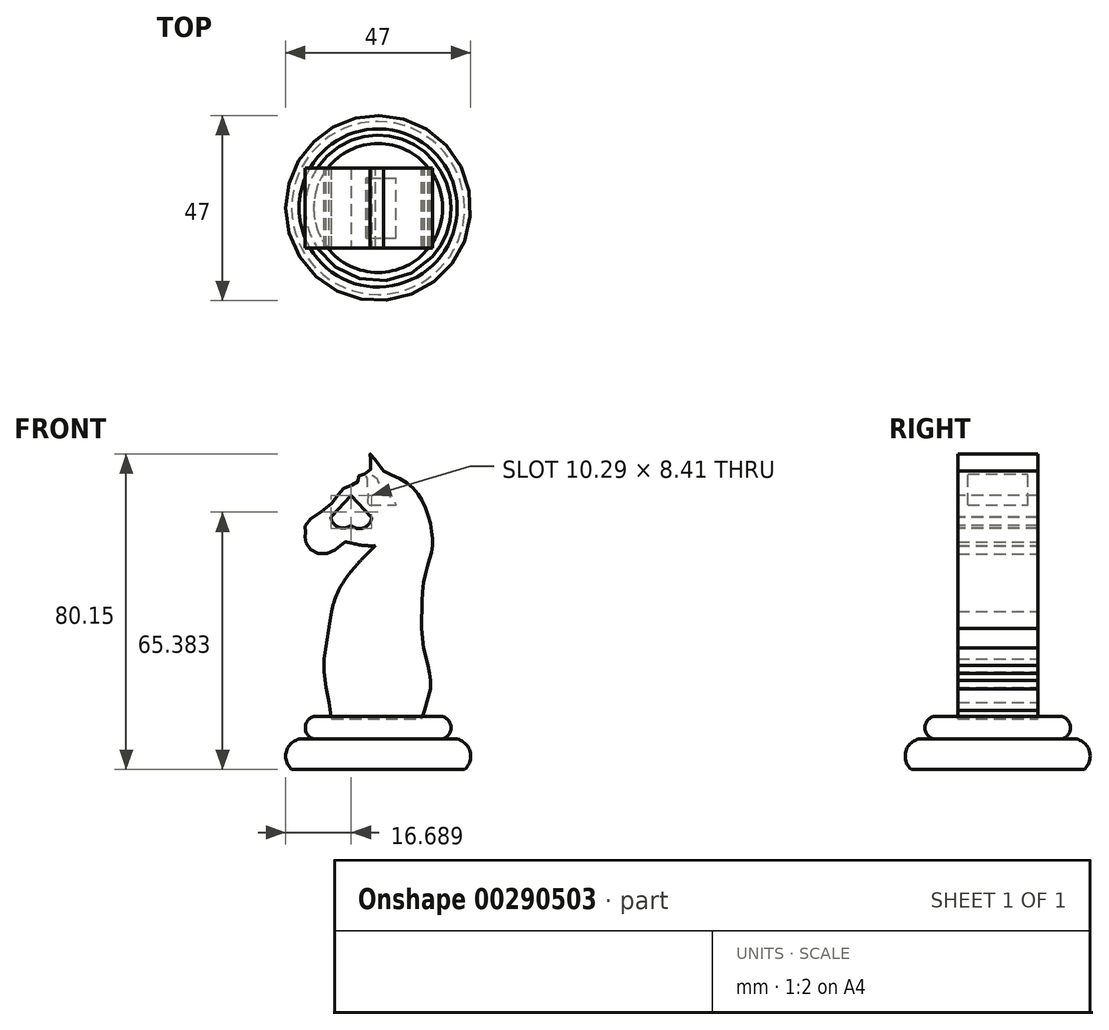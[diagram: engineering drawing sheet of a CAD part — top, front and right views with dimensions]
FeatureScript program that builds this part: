
annotation { "Feature Type Name" : "Feature", "Feature Type Description" : "" }
export const myFeature = defineFeature(function(context is Context, id is Id, definition is map)
    precondition{}
    {
        {
            var Q0;
            Q0=qCreatedBy(makeId("Front.planeOp"),FACE);
            var sketch = newSketch(context, id + "F0", { "sketchPlane" : qUnion([Q0])});
            skArc(sketch, "E0", {"start": v(-7.91, 12.56) * mm, "mid": v(-4.66, 11.9) * mm, "end": v(-2.68, 14.57) * mm});
            skArc(sketch, "E1", {"start": v(-12.98, 14.73) * mm, "mid": v(-11.11, 12.1) * mm, "end": v(-7.91, 12.56) * mm});
            skLineSegment(sketch, "E2", {"start": v(-2.68, 14.57) * mm, "end": v(-7.91, 20.12) * mm});
            skLineSegment(sketch, "E3", {"start": v(-7.91, 20.12) * mm, "end": v(-12.98, 14.73) * mm});
            skSolve(sketch);
        }
        {
            var Q0;
            Q0=qCreatedBy(makeId("Front.planeOp"),FACE);
            var sketch = newSketch(context, id + "F1", { "sketchPlane" : qUnion([Q0])});
            skFitSpline(sketch, "E4", {"points": [v(10.03, -13.65) * mm, v(10.07, -10.39) * mm, v(10.65, -1.4) * mm, v(12.36, 5) * mm, v(12.72, 10.14) * mm, v(11, 16.98) * mm, v(7.45, 22.46) * mm, v(0.32, 26.3) * mm], "startDerivative": vector(-2.98, 24.85) * mm, "endDerivative": vector(-48.92, 20.58) * mm});
            skPoint(sketch, "E5.2.internal.snap0", {"position": v(-3.12, 30.6) * mm});
            skFitSpline(sketch, "E5", {"points": [v(0.32, 26.3) * mm, v(-3.12, 30.6) * mm, v(-3.12, 26.3) * mm, v(-5.87, 25.2) * mm, v(-6.22, 23.55) * mm, v(-9.57, 22.05) * mm, v(-13.06, 17.92) * mm, v(-19.47, 12.65) * mm, v(-19.4, 10.51) * mm, v(-19.62, 9.3) * mm, v(-18.26, 6.45) * mm, v(-14.13, 5.38) * mm, v(-10.85, 7.16) * mm, v(-9.5, 8.23) * mm, v(-5.72, 7.59) * mm, v(-1.73, 7.38) * mm], "startDerivative": vector(-65.76, 86.9) * mm, "endDerivative": vector(54.48, 1.25) * mm});
            skLineSegment(sketch, "E6", {"start": v(-6.37, 2.6) * mm, "end": v(-9.5, 8.23) * mm});
            skLineSegment(sketch, "E7", {"start": v(-12.83, -36.6) * mm, "end": v(10.03, -36.6) * mm});
            skLineSegment(sketch, "E8", {"start": v(-12.83, -9.3) * mm, "end": v(-13.43, -13.22) * mm});
            skLineSegment(sketch, "E9", {"start": v(-13.43, -13.22) * mm, "end": v(-14.7, -21.38) * mm});
            skLineSegment(sketch, "E10", {"start": v(-14.7, -21.38) * mm, "end": v(-14.7, -24.75) * mm});
            skLineSegment(sketch, "E11", {"start": v(-14.7, -24.75) * mm, "end": v(-14.23, -28.6) * mm});
            skLineSegment(sketch, "E12", {"start": v(-14.23, -28.6) * mm, "end": v(-13.54, -32.4) * mm});
            skLineSegment(sketch, "E13", {"start": v(-13.54, -32.4) * mm, "end": v(-12.83, -36.6) * mm});
            skLineSegment(sketch, "E14", {"start": v(12.04, -25.03) * mm, "end": v(11.65, -23.06) * mm});
            skLineSegment(sketch, "E15", {"start": v(11.65, -23.06) * mm, "end": v(10.56, -18.55) * mm});
            skLineSegment(sketch, "E16", {"start": v(10.56, -18.55) * mm, "end": v(10.03, -13.65) * mm});
            skFitSpline(sketch, "E17", {"points": [v(-12.83, -9.3) * mm, v(-11.29, -4.57) * mm, v(-9.35, -1.12) * mm, v(-6.37, 2.6) * mm, v(-1.73, 7.38) * mm], "startDerivative": vector(1.98, 16.57) * mm, "endDerivative": vector(17.28, 17.22) * mm});
            skLineSegment(sketch, "E18", {"start": v(10.03, -36.6) * mm, "end": v(10.76, -34.51) * mm});
            skLineSegment(sketch, "E19", {"start": v(10.76, -34.51) * mm, "end": v(12.24, -29.07) * mm});
            skLineSegment(sketch, "E20", {"start": v(12.24, -29.07) * mm, "end": v(12.24, -26.82) * mm});
            skLineSegment(sketch, "E21", {"start": v(12.24, -26.82) * mm, "end": v(12.04, -25.03) * mm});
            skSolve(sketch);
        }
        {
            var Q0;
            Q0=makeQuery(id+"F1.imprint","IMPRINT",FACE,{"disambiguationData":[TD([[makeQuery(id+"F1.imprint","IMPRINT",EDGE,{"derivedFrom":sQuery(id+"F1.wireOp",EDGE,"E4")}),1.0]])]});
            extrude(context, id + "F2", {"entities" : qUnion([Q0]), "endBound" : BoundingType.SYMMETRIC, "depth" : 20.32 * mm});
        }
        {
            var Q0;
            Q0=makeQuery(id+"F0.imprint","IMPRINT",FACE,{"disambiguationData":[TD([[makeQuery(id+"F0.imprint","IMPRINT",EDGE,{"derivedFrom":sQuery(id+"F0.wireOp",EDGE,"E0")}),1.0]])]});
            var Q1;
            Q1=sQuery(id+"F0.wireOp",EDGE,"E0");
            var Q2;
            Q2=sQuery(id+"F0.wireOp",EDGE,"E1");
            var Q3;
            Q3=sQuery(id+"F0.wireOp",EDGE,"E2");
            var Q4;
            Q4=sQuery(id+"F0.wireOp",EDGE,"E3");
            extrude(context, id + "F3", {"entities" : qUnion([Q0]), "operationType" : NewBodyOperationType.REMOVE, "surfaceEntities" : qUnion([Q1, Q2, Q3, Q4]), "endBound" : BoundingType.SYMMETRIC, "oppositeDirection" : true, "depth" : 25.4 * mm});
        }
        {
            var Q0;
            Q0=qCreatedBy(makeId("Front.planeOp"),FACE);
            var sketch = newSketch(context, id + "F4", { "sketchPlane" : qUnion([Q0])});
            skLineSegment(sketch, "E22", {"start": v(-3.28, 17.74) * mm, "end": v(3.47, 17.74) * mm});
            skFitSpline(sketch, "E23", {"points": [v(-3.28, 17.74) * mm, v(-3.57, 18.3) * mm, v(-3.52, 19.3) * mm, v(-3.5, 20.87) * mm, v(-3.67, 22.36) * mm, v(-3.75, 23.96) * mm, v(-3.74, 24.6) * mm, v(-4.08, 25.22) * mm, v(-3.34, 25.58) * mm, v(-2.88, 25.5) * mm, v(-2.19, 25.09) * mm, v(-1.34, 24.55) * mm, v(-1.18, 23.76) * mm, v(-0.44, 22.97) * mm, v(0.31, 22.16) * mm, v(1.06, 21.13) * mm, v(2.35, 19.44) * mm, v(3.47, 17.74) * mm], "startDerivative": vector(7.08, 8.48) * mm, "endDerivative": vector(2.1, -34.66) * mm});
            skSolve(sketch);
        }
        {
            var Q0;
            Q0=makeQuery(id+"F4.imprint","IMPRINT",FACE,{"disambiguationData":[TD([[makeQuery(id+"F4.imprint","IMPRINT",EDGE,{"derivedFrom":sQuery(id+"F4.wireOp",EDGE,"E22")}),1.0]])]});
            var Q1;
            Q1=sQuery(id+"F4.wireOp",EDGE,"E23");
            var Q2;
            Q2=sQuery(id+"F4.wireOp",EDGE,"E22");
            extrude(context, id + "F5", {"entities" : qUnion([Q0]), "operationType" : NewBodyOperationType.REMOVE, "surfaceEntities" : qUnion([Q1, Q2]), "endBound" : BoundingType.SYMMETRIC, "depth" : 15.24 * mm});
        }
        {
            var Q0;
            Q0=qCreatedBy(makeId("Front.planeOp"),FACE);
            var sketch = newSketch(context, id + "F6", { "sketchPlane" : qUnion([Q0])});
            skLineSegment(sketch, "E24", {"start": v(-1.02, -49.47) * mm, "end": v(19.07, -49.47) * mm});
            skPoint(sketch, "E25.endSnap0", {"position": v(15.36, -41.76) * mm});
            skLineSegment(sketch, "E26", {"start": v(15.36, -36.05) * mm, "end": v(10.54, -36.05) * mm});
            skLineSegment(sketch, "E27", {"start": v(15.36, -41.76) * mm, "end": v(19.07, -41.76) * mm});
            skArc(sketch, "E28", {"start": v(15.36, -41.76) * mm, "mid": v(17.49, -38.9) * mm, "end": v(15.36, -36.05) * mm});
            skLineSegment(sketch, "E29", {"start": v(19.07, -49.47) * mm, "end": v(20.95, -49.47) * mm});
            skArc(sketch, "E30", {"start": v(20.95, -49.47) * mm, "mid": v(22.36, -45.04) * mm, "end": v(19.07, -41.76) * mm});
            skLineSegment(sketch, "E31", {"start": v(10.54, -36.05) * mm, "end": v(-1.02, -36.05) * mm});
            skLineSegment(sketch, "E32", {"start": v(-1.02, -55.58) * mm, "end": v(-1.02, 36.81) * mm});
            skSolve(sketch);
        }
        {
            var Q0;
            {var subQ0=sQuery(id+"F6.wireOp",EDGE,"E24");Q0=makeQuery(id+"F6.imprint","IMPRINT",FACE,{"disambiguationData":[TD([[makeQuery(id+"F6.imprint","IMPRINT",EDGE,{"derivedFrom":subQ0}),1.0]])]});}
            var Q1;
            Q1=sQuery(id+"F6.wireOp",EDGE,"E32");
            revolve(context, id + "F7", {"entities" : qUnion([Q0]), "axis" : qUnion([Q1]), "revolveType" : RevolveType.FULL});
        }
    });
